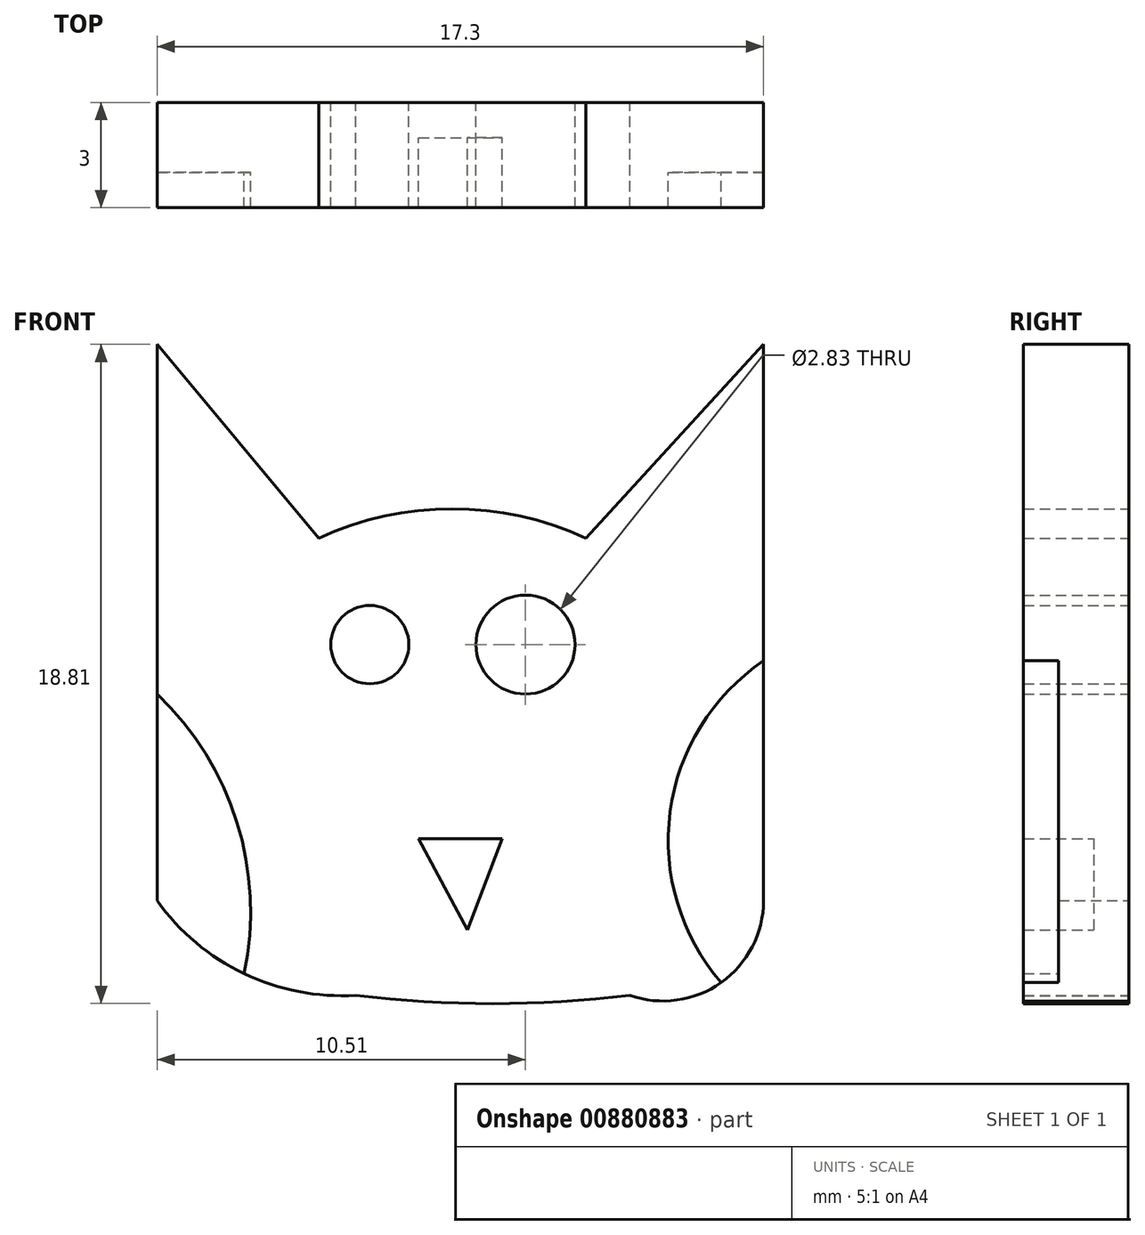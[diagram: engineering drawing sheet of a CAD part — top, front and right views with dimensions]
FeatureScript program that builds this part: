
annotation { "Feature Type Name" : "Feature", "Feature Type Description" : "" }
export const myFeature = defineFeature(function(context is Context, id is Id, definition is map)
    precondition{}
    {
        {
            var Q0;
            Q0=qCreatedBy(makeId("Front.planeOp"),FACE);
            var sketch = newSketch(context, id + "F0", { "sketchPlane" : qUnion([Q0])});
            skLineSegment(sketch, "E0", {"start": v(-18.97, 3.96) * mm, "end": v(-18.97, -10.34) * mm});
            skArc(sketch, "E1", {"start": v(-18.97, -10.34) * mm, "mid": v(-16.5, -12.43) * mm, "end": v(-13.3, -13.04) * mm});
            skArc(sketch, "E2", {"start": v(-13.3, -13.04) * mm, "mid": v(-9.4, -13.28) * mm, "end": v(-5.49, -13.04) * mm});
            skLineSegment(sketch, "E3", {"start": v(-1.67, -10.34) * mm, "end": v(-1.67, 5.53) * mm});
            skLineSegment(sketch, "E4", {"start": v(-1.67, 5.53) * mm, "end": v(-6.74, 0) * mm});
            skLineSegment(sketch, "E5", {"start": v(-18.97, 3.96) * mm, "end": v(-18.97, 5.53) * mm});
            skArc(sketch, "E6", {"start": v(-6.74, 0) * mm, "mid": v(-10.55, 0.84) * mm, "end": v(-14.36, 0) * mm});
            skLineSegment(sketch, "E7", {"start": v(-14.36, 0) * mm, "end": v(-18.97, 5.53) * mm});
            skArc(sketch, "E8", {"start": v(-1.67, -3.5) * mm, "mid": v(-4.34, -7.82) * mm, "end": v(-2.88, -12.68) * mm});
            skArc(sketch, "E9", {"start": v(-16.5, -12.43) * mm, "mid": v(-16.7, -8.11) * mm, "end": v(-18.97, -4.45) * mm});
            skArc(sketch, "E10", {"start": v(-5.49, -13.04) * mm, "mid": v(-2.88, -12.68) * mm, "end": v(-1.67, -10.34) * mm});
            skCircle(sketch, "E11", {"center": v(-12.9, -3.04) * mm, "radius": 1.12 * mm});
            skCircle(sketch, "E12", {"center": v(-8.46, -3.04) * mm, "radius": 1.41 * mm});
            skLineSegment(sketch, "E13", {"start": v(-11.51, -8.58) * mm, "end": v(-10.12, -11.18) * mm});
            skLineSegment(sketch, "E14", {"start": v(-9.12, -8.57) * mm, "end": v(-10.12, -11.18) * mm});
            skLineSegment(sketch, "E15", {"start": v(-11.51, -8.58) * mm, "end": v(-9.12, -8.57) * mm});
            skSolve(sketch);
        }
        {
            var Q0;
            {var subQ5=sQuery(id+"F0.wireOp",EDGE,"E2");Q0=makeQuery(id+"F0.imprint","IMPRINT",FACE,{"disambiguationData":[TD([[makeQuery(id+"F0.imprint","IMPRINT",EDGE,{"derivedFrom":subQ5}),1.0]])]});}
            extrude(context, id + "F1", {"entities" : qUnion([Q0]), "depth" : 3 * mm, "offsetDistance" : 25 * mm});
        }
        {
            var Q0;
            {var subQ3=sQuery(id+"F0.wireOp",EDGE,"E9");Q0=makeQuery(id+"F0.imprint","IMPRINT",FACE,{"disambiguationData":[TD([[makeQuery(id+"F0.imprint","IMPRINT",EDGE,{"derivedFrom":subQ3}),1.0]])]});}
            var Q1;
            {var subQ3=sQuery(id+"F0.wireOp",EDGE,"E8");Q1=makeQuery(id+"F0.imprint","IMPRINT",FACE,{"disambiguationData":[TD([[makeQuery(id+"F0.imprint","IMPRINT",EDGE,{"derivedFrom":subQ3}),1.0]])]});}
            extrude(context, id + "F2", {"entities" : qUnion([Q0, Q1]), "operationType" : NewBodyOperationType.ADD, "depth" : 2 * mm, "offsetDistance" : 25 * mm});
        }
        {
            var Q0;
            Q0=makeQuery(id+"F0.imprint","IMPRINT",FACE,{"disambiguationData":[TD([[makeQuery(id+"F0.imprint","IMPRINT",EDGE,{"derivedFrom":sQuery(id+"F0.wireOp",EDGE,"E13")}),1.0]])]});
            extrude(context, id + "F3", {"entities" : qUnion([Q0]), "operationType" : NewBodyOperationType.ADD, "depth" : 1 * mm, "offsetDistance" : 25 * mm});
        }
    });
